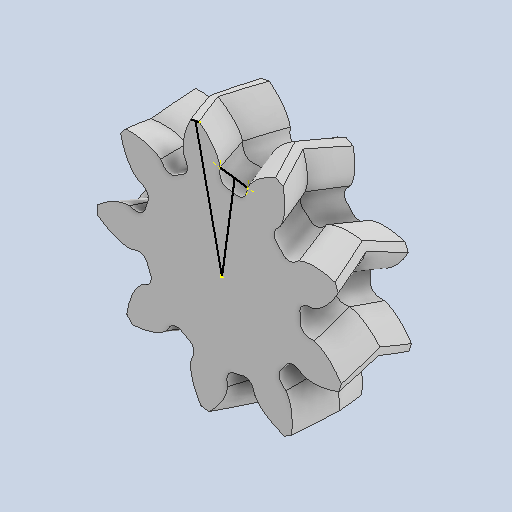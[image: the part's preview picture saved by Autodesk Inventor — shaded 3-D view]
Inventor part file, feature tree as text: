
AUTODESK INVENTOR PART (.ipt)
format: ipt  version: 2022 (Build 260153070, 153G)  size: 571,904 bytes
history: native  units: mm
features: sketch x2, extrude x1, helix x1, pattern_circular x1, mirror x1
ambient origin geometry x8: Origin, YZ Plane, XZ Plane, XY Plane, X Axis, Y Axis, Z Axis, Center Point
bodies: Solid1 (feature_tree)
feature tree (6):
  sketch  "Sketch1"  dims[d0=1.5mm d1=0.0mm]
  extrude  "Extrusion1"  TaperAngle=0.0deg  [1 undecoded]
  helix  "Coil1"  [1 undecoded]
  pattern_circular  "Circular Pattern1"  [2 undecoded]
  mirror  "Mirror1"
  sketch  "Sketch3"  dims[d2=70.268674mm d3=1.5mm d4=10.0mm d5=0.0mm d6=90.0deg d7=90.0deg d8=0.0mm d9=0.0mm d10=90.0mm d11=360.0deg]
note: 4 required parameter values undecoded (feature->parameter linkage not recoverable at this tier; creation-order binding heuristic only, values carry confidence <= 0.55)
